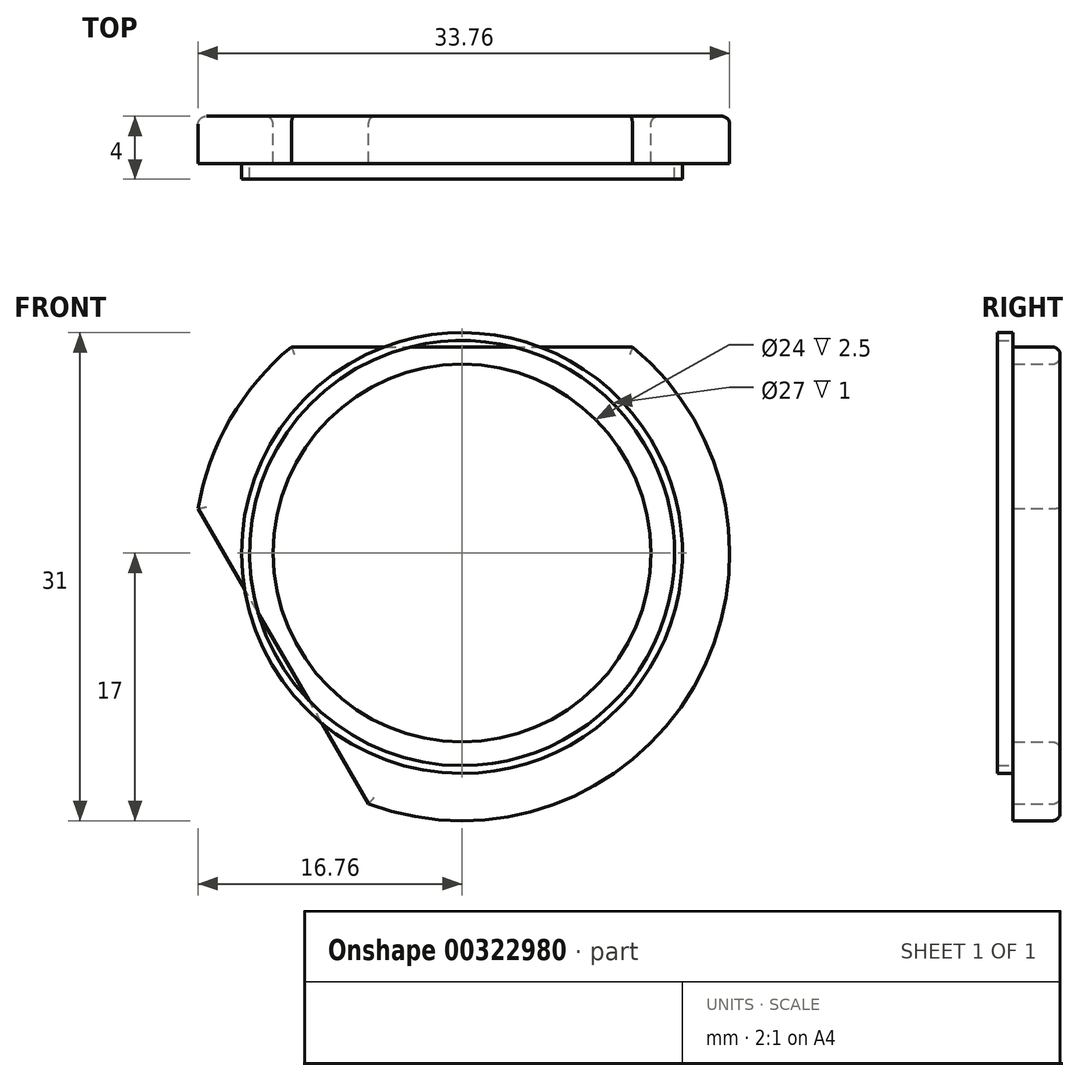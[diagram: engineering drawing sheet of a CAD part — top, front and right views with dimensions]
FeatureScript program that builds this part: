
annotation { "Feature Type Name" : "Feature", "Feature Type Description" : "" }
export const myFeature = defineFeature(function(context is Context, id is Id, definition is map)
    precondition{}
    {
        {
            var Q0;
            Q0=qCreatedBy(makeId("Front.planeOp"),FACE);
            var sketch = newSketch(context, id + "F0", { "sketchPlane" : qUnion([Q0])});
            skCircle(sketch, "E0", {"center": v(0, 0) * mm, "radius": 12 * mm});
            skCircle(sketch, "E1", {"center": v(0, 0) * mm, "radius": 17 * mm});
            skCircle(sketch, "E2", {"center": v(0, 0) * mm, "radius": 14.5 * mm, "construction": true});
            skCircle(sketch, "E3", {"center": v(0, 0) * mm, "radius": 19 * mm, "construction": true});
            skCircle(sketch, "E4", {"center": v(0, 0) * mm, "radius": 21 * mm, "construction": true});
            skLineSegment(sketch, "E5", {"start": v(0, 0) * mm, "end": v(0, 23.44) * mm, "construction": true});
            skLineSegment(sketch, "E6.0", {"start": v(0, 14.5) * mm, "end": v(12.56, -7.25) * mm, "construction": true});
            skLineSegment(sketch, "E6.1", {"start": v(12.56, -7.25) * mm, "end": v(-12.56, -7.25) * mm, "construction": true});
            skLineSegment(sketch, "E6.2", {"start": v(-12.56, -7.25) * mm, "end": v(0, 14.5) * mm, "construction": true});
            skLineSegment(sketch, "E7", {"start": v(0, 0) * mm, "end": v(0, -20.5) * mm, "construction": true});
            skPoint(sketch, "E7.endSnap0", {"position": v(0, -7.25) * mm});
            skLineSegment(sketch, "E8.0", {"start": v(0, -19) * mm, "end": v(-16.45, 9.5) * mm, "construction": true});
            skLineSegment(sketch, "E8.1", {"start": v(-16.45, 9.5) * mm, "end": v(16.45, 9.5) * mm, "construction": true});
            skLineSegment(sketch, "E8.2", {"start": v(16.45, 9.5) * mm, "end": v(0, -19) * mm, "construction": true});
            skLineSegment(sketch, "E9.0", {"start": v(-16.45, 13.1) * mm, "end": v(16.45, 13.1) * mm});
            skLineSegment(sketch, "E10.0", {"start": v(-3.12, -20.8) * mm, "end": v(-19.57, 7.7) * mm});
            skLineSegment(sketch, "E11.0", {"start": v(19.57, 7.7) * mm, "end": v(3.12, -20.8) * mm});
            skArc(sketch, "E12", {"start": v(-19.57, 7.7) * mm, "mid": v(-18.21, 10.52) * mm, "end": v(-16.45, 13.1) * mm});
            skArc(sketch, "E13", {"start": v(16.45, 13.1) * mm, "mid": v(18.21, 10.52) * mm, "end": v(19.57, 7.7) * mm});
            skArc(sketch, "E14", {"start": v(3.12, -20.8) * mm, "mid": v(0, -21.03) * mm, "end": v(-3.12, -20.8) * mm});
            skSolve(sketch);
        }
        {
            var Q0;
            {var subQ5=sQuery(id+"F0.wireOp",EDGE,"E12");Q0=makeQuery(id+"F0.imprint","IMPRINT",FACE,{"disambiguationData":[TD([[makeQuery(id+"F0.imprint","IMPRINT",EDGE,{"derivedFrom":subQ5}),-1.0]])]});}
            var Q1;
            Q1=makeQuery(id+"F0.imprint","IMPRINT",FACE,{"disambiguationData":[TD([[makeQuery(id+"F0.imprint","IMPRINT",EDGE,{"derivedFrom":sQuery(id+"F0.wireOp",EDGE,"E0")}),-1.0]])]});
            var Q2;
            {var subQ5=sQuery(id+"F0.wireOp",EDGE,"E14");Q2=makeQuery(id+"F0.imprint","IMPRINT",FACE,{"disambiguationData":[TD([[makeQuery(id+"F0.imprint","IMPRINT",EDGE,{"derivedFrom":subQ5}),-1.0]])]});}
            var Q3;
            {var subQ5=sQuery(id+"F0.wireOp",EDGE,"E13");Q3=makeQuery(id+"F0.imprint","IMPRINT",FACE,{"disambiguationData":[TD([[makeQuery(id+"F0.imprint","IMPRINT",EDGE,{"derivedFrom":subQ5}),-1.0]])]});}
            var Q4;
            {var subQ0=sQuery(id+"F0.wireOp",EDGE,"E9.0");var subQ1=sQuery(id+"F0.wireOp",EDGE,"E1");var subQ2=makeQuery(id+"F0.imprint","INTERSECT",VERTEX,{"disambiguationData":[OD(0.0)],"derivedFrom":[subQ1,subQ0]});Q4=makeQuery(id+"F0.imprint","IMPRINT",FACE,{"disambiguationData":[TD([[makeQuery(id+"F0.imprint","IMPRINT",EDGE,{"disambiguationData":[TD([[subQ2,-1.0]])],"derivedFrom":subQ1}),1.0]])]});}
            var Q5;
            {var subQ0=sQuery(id+"F0.wireOp",EDGE,"E11.0");var subQ1=sQuery(id+"F0.wireOp",EDGE,"E1");var subQ2=makeQuery(id+"F0.imprint","INTERSECT",VERTEX,{"disambiguationData":[OD(0.0)],"derivedFrom":[subQ1,subQ0]});Q5=makeQuery(id+"F0.imprint","IMPRINT",FACE,{"disambiguationData":[TD([[makeQuery(id+"F0.imprint","IMPRINT",EDGE,{"disambiguationData":[TD([[subQ2,1.0]])],"derivedFrom":subQ1}),1.0]])]});}
            var Q6;
            {var subQ0=sQuery(id+"F0.wireOp",EDGE,"E10.0");var subQ1=sQuery(id+"F0.wireOp",EDGE,"E1");var subQ2=makeQuery(id+"F0.imprint","INTERSECT",VERTEX,{"disambiguationData":[OD(0.0)],"derivedFrom":[subQ1,subQ0]});Q6=makeQuery(id+"F0.imprint","IMPRINT",FACE,{"disambiguationData":[TD([[makeQuery(id+"F0.imprint","IMPRINT",EDGE,{"disambiguationData":[TD([[subQ2,-1.0]])],"derivedFrom":subQ1}),1.0]])]});}
            extrude(context, id + "F1", {"entities" : qUnion([Q0, Q1, Q2, Q3, Q4, Q5, Q6]), "depth" : 3 * mm});
        }
        {
            var Q0;
            Q0=sQuery(id+"F0.wireOp",VERTEX,"E8.1.start");
            var Q1;
            Q1=sQuery(id+"F0.wireOp",VERTEX,"E8.2.start");
            var Q2;
            Q2=sQuery(id+"F0.wireOp",VERTEX,"E8.0.start");
            var Q3;
            Q3=makeQuery(id+"F1.opExtrude","SWEPT_BODY",BODY,{"disambiguationData":[OSD([sQuery(id+"F0.wireOp",EDGE,"E0"),sQuery(id+"F0.wireOp",EDGE,"E1"),sQuery(id+"F0.wireOp",EDGE,"E9.0"),sQuery(id+"F0.wireOp",EDGE,"E10.0"),sQuery(id+"F0.wireOp",EDGE,"E11.0"),sQuery(id+"F0.wireOp",EDGE,"E12"),sQuery(id+"F0.wireOp",EDGE,"E13"),sQuery(id+"F0.wireOp",EDGE,"E14")])]});
            hole(context, id + "F2", {"style" : HoleStyle.SIMPLE, "endStyle" : HoleEndStyle.THROUGH, "oppositeDirection" : true, "standardTappedOrClearance" : lookupTablePath({ "standard" : "ISO", "fit" : "Normal", "size" : "M3", "type" : "Clearance" }), "standardBlindInLast" : lookupTablePath({ "fit" : "Standard", "standard" : "ISO", "size" : "M3", "type" : "Clearance" }), "holeDiameter" : 3.3 * mm, "isTappedThrough" : true, "tappedDepth" : 12 * mm, "tapClearance" : 3, "startFromSketch" : true, "locations" : qUnion([Q0, Q1, Q2]), "scope" : qUnion([Q3])});
        }
        {
            var Q0;
            {var subQ0=sQuery(id+"F0.wireOp",EDGE,"E10.0");var subQ1=sQuery(id+"F0.wireOp",EDGE,"E1");Q0=makeQuery(id+"F1.opExtrude","CAP_EDGE",EDGE,{"disambiguationData":[OSD([subQ1]),TDD([makeQuery(id+"F0.imprint","IMPRINT",EDGE,{"disambiguationData":[TD([[makeQuery(id+"F0.imprint","INTERSECT",VERTEX,{"disambiguationData":[OD(0.0)],"derivedFrom":[subQ1,subQ0]}),-1.0]])],"derivedFrom":subQ1})])],"isStart":true});}
            var Q1;
            {var subQ0=sQuery(id+"F0.wireOp",EDGE,"E10.0");Q1=makeQuery(id+"F1.opExtrude","CAP_EDGE",EDGE,{"disambiguationData":[OSD([subQ0]),TDD([makeQuery(id+"F0.imprint","IMPRINT",EDGE,{"disambiguationData":[TD([[makeQuery(id+"F0.imprint","INTERSECT",VERTEX,{"derivedFrom":[subQ0,sQuery(id+"F0.wireOp",EDGE,"E14")]}),-1.0]])],"derivedFrom":subQ0})])],"isStart":true});}
            var Q2;
            Q2=makeQuery(id+"F1.opExtrude","CAP_EDGE",EDGE,{"disambiguationData":[OSD([sQuery(id+"F0.wireOp",EDGE,"E14")])],"isStart":true});
            var Q3;
            {var subQ0=sQuery(id+"F0.wireOp",EDGE,"E11.0");Q3=makeQuery(id+"F1.opExtrude","CAP_EDGE",EDGE,{"disambiguationData":[OSD([subQ0]),TDD([makeQuery(id+"F0.imprint","IMPRINT",EDGE,{"disambiguationData":[TD([[makeQuery(id+"F0.imprint","INTERSECT",VERTEX,{"derivedFrom":[subQ0,sQuery(id+"F0.wireOp",EDGE,"E14")]}),1.0]])],"derivedFrom":subQ0})])],"isStart":true});}
            var Q4;
            {var subQ0=sQuery(id+"F0.wireOp",EDGE,"E11.0");var subQ1=sQuery(id+"F0.wireOp",EDGE,"E1");Q4=makeQuery(id+"F1.opExtrude","CAP_EDGE",EDGE,{"disambiguationData":[OSD([subQ1]),TDD([makeQuery(id+"F0.imprint","IMPRINT",EDGE,{"disambiguationData":[TD([[makeQuery(id+"F0.imprint","INTERSECT",VERTEX,{"disambiguationData":[OD(0.0)],"derivedFrom":[subQ1,subQ0]}),1.0]])],"derivedFrom":subQ1})])],"isStart":true});}
            var Q5;
            {var subQ0=sQuery(id+"F0.wireOp",EDGE,"E11.0");Q5=makeQuery(id+"F1.opExtrude","CAP_EDGE",EDGE,{"disambiguationData":[OSD([subQ0]),TDD([makeQuery(id+"F0.imprint","IMPRINT",EDGE,{"disambiguationData":[TD([[makeQuery(id+"F0.imprint","INTERSECT",VERTEX,{"derivedFrom":[subQ0,sQuery(id+"F0.wireOp",EDGE,"E13")]}),-1.0]])],"derivedFrom":subQ0})])],"isStart":true});}
            var Q6;
            Q6=makeQuery(id+"F1.opExtrude","CAP_EDGE",EDGE,{"disambiguationData":[OSD([sQuery(id+"F0.wireOp",EDGE,"E13")])],"isStart":true});
            var Q7;
            {var subQ0=sQuery(id+"F0.wireOp",EDGE,"E9.0");Q7=makeQuery(id+"F1.opExtrude","CAP_EDGE",EDGE,{"disambiguationData":[OSD([subQ0]),TDD([makeQuery(id+"F0.imprint","IMPRINT",EDGE,{"disambiguationData":[TD([[makeQuery(id+"F0.imprint","INTERSECT",VERTEX,{"derivedFrom":[subQ0,sQuery(id+"F0.wireOp",EDGE,"E13")]}),1.0]])],"derivedFrom":subQ0})])],"isStart":true});}
            var Q8;
            Q8=makeQuery(id+"F1.opExtrude","CAP_FACE",FACE,{"disambiguationData":[OSD([sQuery(id+"F0.wireOp",EDGE,"E0"),sQuery(id+"F0.wireOp",EDGE,"E1"),sQuery(id+"F0.wireOp",EDGE,"E9.0"),sQuery(id+"F0.wireOp",EDGE,"E10.0"),sQuery(id+"F0.wireOp",EDGE,"E11.0"),sQuery(id+"F0.wireOp",EDGE,"E12"),sQuery(id+"F0.wireOp",EDGE,"E13"),sQuery(id+"F0.wireOp",EDGE,"E14")])],"isStart":true});
            var Q9;
            {var subQ0=sQuery(id+"F0.wireOp",EDGE,"E9.0");Q9=makeQuery(id+"F1.opExtrude","CAP_EDGE",EDGE,{"disambiguationData":[OSD([subQ0]),TDD([makeQuery(id+"F0.imprint","IMPRINT",EDGE,{"disambiguationData":[TD([[makeQuery(id+"F0.imprint","INTERSECT",VERTEX,{"derivedFrom":[subQ0,sQuery(id+"F0.wireOp",EDGE,"E12")]}),-1.0]])],"derivedFrom":subQ0})])],"isStart":true});}
            var Q10;
            Q10=makeQuery(id+"F1.opExtrude","CAP_EDGE",EDGE,{"disambiguationData":[OSD([sQuery(id+"F0.wireOp",EDGE,"E12")])],"isStart":true});
            fillet(context, id + "F3", {"entities" : qUnion([Q0, Q1, Q2, Q3, Q4, Q5, Q6, Q7, Q8, Q9, Q10]), "radius" : .5 * mm, "tangentPropagation" : true, "allowEdgeOverflow" : false});
        }
        {
            var Q0;
            Q0=makeQuery(id+"F1.opExtrude","CAP_FACE",FACE,{"disambiguationData":[OSD([sQuery(id+"F0.wireOp",EDGE,"E0"),sQuery(id+"F0.wireOp",EDGE,"E1"),sQuery(id+"F0.wireOp",EDGE,"E9.0"),sQuery(id+"F0.wireOp",EDGE,"E10.0"),sQuery(id+"F0.wireOp",EDGE,"E11.0"),sQuery(id+"F0.wireOp",EDGE,"E12"),sQuery(id+"F0.wireOp",EDGE,"E13"),sQuery(id+"F0.wireOp",EDGE,"E14")])],"isStart":false});
            var sketch = newSketch(context, id + "F4", { "sketchPlane" : qUnion([Q0])});
            skCircle(sketch, "E15", {"center": v(0, 0) * mm, "radius": 13.5 * mm});
            skCircle(sketch, "E16", {"center": v(0, 0) * mm, "radius": 14 * mm});
            skSolve(sketch);
        }
        {
            var Q0;
            Q0=makeQuery(id+"F4.imprint","IMPRINT",FACE,{"disambiguationData":[TD([[makeQuery(id+"F4.imprint","IMPRINT",EDGE,{"derivedFrom":sQuery(id+"F4.wireOp",EDGE,"E15")}),-1.0]])]});
            extrude(context, id + "F5", {"entities" : qUnion([Q0]), "operationType" : NewBodyOperationType.ADD, "depth" : 1 * mm});
        }
    });
